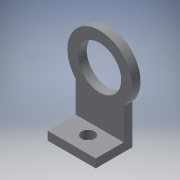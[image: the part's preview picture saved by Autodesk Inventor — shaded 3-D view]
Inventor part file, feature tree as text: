
AUTODESK INVENTOR PART (.ipt)
format: ipt  version: 2016 (Build 200138000, 138)  size: 131,072 bytes
history: native  units: in
note: dims shown in document units (in); Inventor stores cm internally (conversion verified against a paired STEP export)
features: extrude x4, sketch x4, reference x2
ambient origin geometry x8: Origin, YZ Plane, XZ Plane, XY Plane, X Axis, Y Axis, Z Axis, Center Point
bodies: Solid1 (feature_tree)
feature tree (10):
  extrude  "Extrusion1"  Depth=0.3937in
  extrude  "Extrusion2"  Depth=0.0787in TaperAngle=0.0deg
  extrude  "Extrusion5"  Depth=0.3346in
  extrude  "Extrusion6"  Depth=0.0787in
  sketch  "Sketch1"  dims[d0=0.3937in d1=0.5906in]
  reference  "Reference1"
  sketch  "Sketch2"  dims[d2=0.0787in d3=0.0in d4=0.0787in d5=0.0in]
  reference  "Reference2"
  sketch  "Sketch5"  dims[d13=0.0984in d14=0.3346in]
  sketch  "Sketch6"  dims[d15=0.0787in d16=0.0in d17=0.15in d18=0.1181in d19=0.0787in d20=0.0in]
